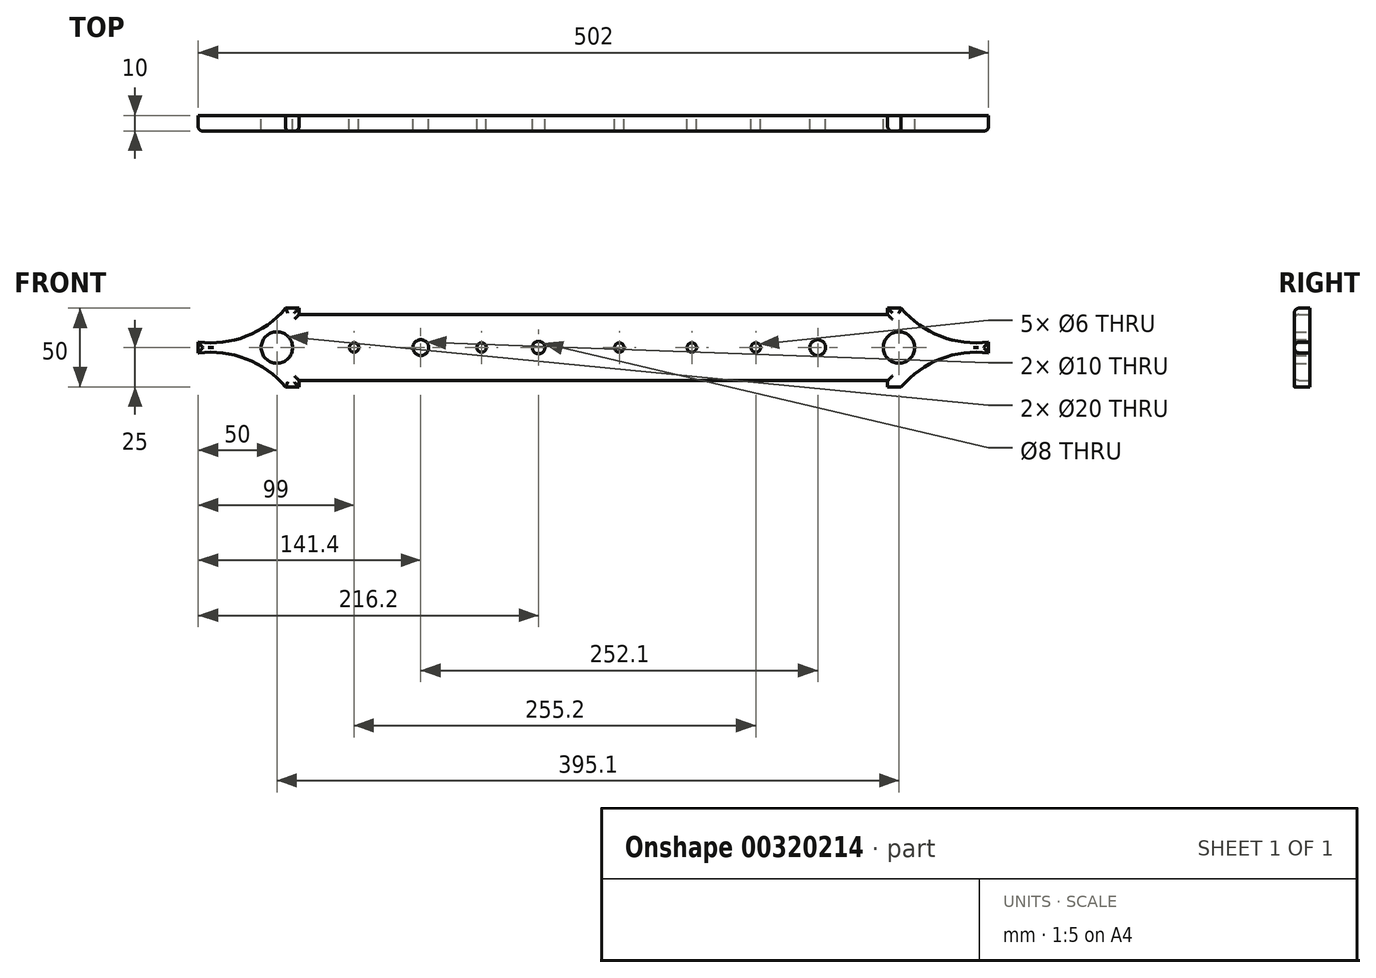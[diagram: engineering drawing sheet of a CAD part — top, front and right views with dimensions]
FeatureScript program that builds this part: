
annotation { "Feature Type Name" : "Feature", "Feature Type Description" : "" }
export const myFeature = defineFeature(function(context is Context, id is Id, definition is map)
    precondition{}
    {
        {
            var Q0;
            Q0=qCreatedBy(makeId("Front.planeOp"),FACE);
            var sketch = newSketch(context, id + "F0", { "sketchPlane" : qUnion([Q0])});
            skLineSegment(sketch, "E0", {"start": v(-251, 0) * mm, "end": v(251, 0) * mm, "construction": true});
            skArc(sketch, "E1", {"start": v(195.5, 25) * mm, "mid": v(220.5, 7.17) * mm, "end": v(251, 3.5) * mm});
            skLineSegment(sketch, "E2", {"start": v(195.5, 25) * mm, "end": v(186.9, 25) * mm});
            skLineSegment(sketch, "E3", {"start": v(186.9, 25) * mm, "end": v(186.9, 21) * mm});
            skArc(sketch, "E4.MirrorCS", {"start": v(195.5, -25) * mm, "mid": v(220.5, -7.17) * mm, "end": v(251, -3.5) * mm});
            skLineSegment(sketch, "E5.MirrorCS", {"start": v(195.5, -25) * mm, "end": v(186.9, -25) * mm});
            skLineSegment(sketch, "E6.MirrorCS", {"start": v(186.9, -25) * mm, "end": v(186.9, -21) * mm});
            skLineSegment(sketch, "E7", {"start": v(251, 3.5) * mm, "end": v(251, -3.5) * mm});
            skLineSegment(sketch, "E8.MirrorCS", {"start": v(-195.5, -25) * mm, "end": v(-186.9, -25) * mm});
            skLineSegment(sketch, "E9.MirrorCS", {"start": v(-186.9, -25) * mm, "end": v(-186.9, -21) * mm});
            skArc(sketch, "E10.MirrorCS", {"start": v(-195.5, -25) * mm, "mid": v(-220.5, -7.17) * mm, "end": v(-251, -3.5) * mm});
            skLineSegment(sketch, "E11.MirrorCS", {"start": v(-251, 3.5) * mm, "end": v(-251, -3.5) * mm});
            skArc(sketch, "E12.MirrorCS", {"start": v(-195.5, 25) * mm, "mid": v(-220.5, 7.17) * mm, "end": v(-251, 3.5) * mm});
            skLineSegment(sketch, "E13.MirrorCS", {"start": v(-195.5, 25) * mm, "end": v(-186.9, 25) * mm});
            skLineSegment(sketch, "E14.MirrorCS", {"start": v(-186.9, 25) * mm, "end": v(-186.9, 21) * mm});
            skLineSegment(sketch, "E15", {"start": v(-186.9, -21) * mm, "end": v(186.9, -21) * mm});
            skLineSegment(sketch, "E16", {"start": v(-186.9, 21) * mm, "end": v(186.9, 21) * mm});
            skPoint(sketch, "E17.orphan", {"position": v(-40.13, 0) * mm});
            skCircle(sketch, "E18", {"center": v(-201, 0) * mm, "radius": 10 * mm});
            skCircle(sketch, "E19", {"center": v(-152, 0) * mm, "radius": 3 * mm});
            skCircle(sketch, "E20", {"center": v(-109.6, 0) * mm, "radius": 5 * mm});
            skCircle(sketch, "E21", {"center": v(-71, 0) * mm, "radius": 3 * mm});
            skCircle(sketch, "E22", {"center": v(-34.8, 0) * mm, "radius": 4 * mm});
            skCircle(sketch, "E23", {"center": v(16.5, 0) * mm, "radius": 3 * mm});
            skCircle(sketch, "E24", {"center": v(62.5, 0) * mm, "radius": 3 * mm});
            skCircle(sketch, "E25", {"center": v(103.2, 0) * mm, "radius": 3 * mm});
            skCircle(sketch, "E26", {"center": v(142.5, 0) * mm, "radius": 5 * mm});
            skCircle(sketch, "E27", {"center": v(194.1, 0) * mm, "radius": 10 * mm});
            skSolve(sketch);
        }
        {
            var Q0;
            Q0=makeQuery(id+"F0.imprint","IMPRINT",FACE,{"disambiguationData":[TD([[makeQuery(id+"F0.imprint","IMPRINT",EDGE,{"derivedFrom":sQuery(id+"F0.wireOp",EDGE,"E1")}),-1.0]])]});
            extrude(context, id + "F1", {"entities" : qUnion([Q0]), "depth" : 10 * mm});
        }
        {
            var Q0;
            Q0=makeQuery(id+"F1.opExtrude","CAP_EDGE",EDGE,{"disambiguationData":[OSD([sQuery(id+"F0.wireOp",EDGE,"E7")])],"isStart":false});
            var Q1;
            Q1=makeQuery(id+"F1.opExtrude","CAP_EDGE",EDGE,{"disambiguationData":[OSD([sQuery(id+"F0.wireOp",EDGE,"E1")])],"isStart":false});
            var Q2;
            Q2=makeQuery(id+"F1.opExtrude","CAP_EDGE",EDGE,{"disambiguationData":[OSD([sQuery(id+"F0.wireOp",EDGE,"E2")])],"isStart":false});
            var Q3;
            Q3=makeQuery(id+"F1.opExtrude","CAP_EDGE",EDGE,{"disambiguationData":[OSD([sQuery(id+"F0.wireOp",EDGE,"E3")])],"isStart":false});
            var Q4;
            Q4=makeQuery(id+"F1.opExtrude","CAP_EDGE",EDGE,{"disambiguationData":[OSD([sQuery(id+"F0.wireOp",EDGE,"E16")])],"isStart":false});
            var Q5;
            Q5=makeQuery(id+"F1.opExtrude","CAP_EDGE",EDGE,{"disambiguationData":[OSD([sQuery(id+"F0.wireOp",EDGE,"E15")])],"isStart":false});
            var Q6;
            Q6=makeQuery(id+"F1.opExtrude","CAP_EDGE",EDGE,{"disambiguationData":[OSD([sQuery(id+"F0.wireOp",EDGE,"E6.MirrorCS")])],"isStart":false});
            var Q7;
            Q7=makeQuery(id+"F1.opExtrude","CAP_EDGE",EDGE,{"disambiguationData":[OSD([sQuery(id+"F0.wireOp",EDGE,"E4.MirrorCS")])],"isStart":false});
            var Q8;
            Q8=makeQuery(id+"F1.opExtrude","CAP_EDGE",EDGE,{"disambiguationData":[OSD([sQuery(id+"F0.wireOp",EDGE,"E9.MirrorCS")])],"isStart":false});
            var Q9;
            Q9=makeQuery(id+"F1.opExtrude","CAP_EDGE",EDGE,{"disambiguationData":[OSD([sQuery(id+"F0.wireOp",EDGE,"E14.MirrorCS")])],"isStart":false});
            var Q10;
            Q10=makeQuery(id+"F1.opExtrude","CAP_EDGE",EDGE,{"disambiguationData":[OSD([sQuery(id+"F0.wireOp",EDGE,"E11.MirrorCS")])],"isStart":false});
            var Q11;
            Q11=makeQuery(id+"F1.opExtrude","CAP_EDGE",EDGE,{"disambiguationData":[OSD([sQuery(id+"F0.wireOp",EDGE,"E10.MirrorCS")])],"isStart":false});
            var Q12;
            Q12=makeQuery(id+"F1.opExtrude","CAP_EDGE",EDGE,{"disambiguationData":[OSD([sQuery(id+"F0.wireOp",EDGE,"E13.MirrorCS")])],"isStart":false});
            var Q13;
            Q13=makeQuery(id+"F1.opExtrude","CAP_EDGE",EDGE,{"disambiguationData":[OSD([sQuery(id+"F0.wireOp",EDGE,"E12.MirrorCS")])],"isStart":false});
            var Q14;
            Q14=makeQuery(id+"F1.opExtrude","CAP_EDGE",EDGE,{"disambiguationData":[OSD([sQuery(id+"F0.wireOp",EDGE,"E8.MirrorCS")])],"isStart":false});
            fillet(context, id + "F2", {"entities" : qUnion([Q0, Q1, Q2, Q3, Q4, Q5, Q6, Q7, Q8, Q9, Q10, Q11, Q12, Q13, Q14]), "radius" : 3 * mm, "tangentPropagation" : true, "allowEdgeOverflow" : false});
        }
    });
